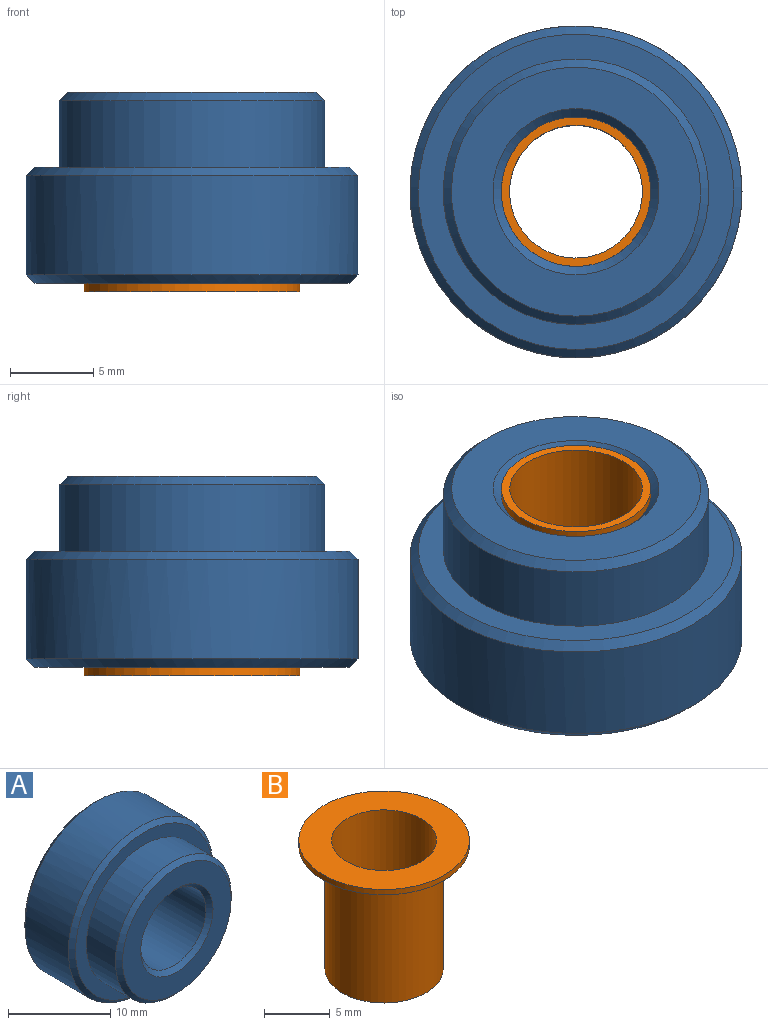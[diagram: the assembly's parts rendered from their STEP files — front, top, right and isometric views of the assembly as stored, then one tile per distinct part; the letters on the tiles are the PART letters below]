
ASSEMBLY  parts=2 mates=1
PART A: 11 faces, bbox 20x11.5x20 mm
  f0: plane 15x15mm, normal (0,-1,0), area 98.2mm2, adj f6,f9
  f1: cylinder r=4.5mm len=10.5mm, axis (0,-1,0), area 296.9mm2, adj f9,f10
  f2: plane 19x19mm, normal (0,1,0), area 205mm2, adj f7,f10
  f3: cylinder r=10mm len=20mm, axis (0,-1,0), area 377mm2, adj f7,f8
  f4: plane 19x19mm, normal (0,-1,0), area 82.5mm2, adj f5,f8
  f5: cylinder r=8mm len=16mm, axis (0,-1,0), area 201.1mm2, adj f4,f6
  f6: cone r=7.5mm half-angle=45deg, axis (0,1,0), area 34.4mm2, adj f0,f5
  f7: cone r=10mm half-angle=45deg, axis (0,-1,0), area 43.3mm2, adj f2,f3
  f8: cone r=9.5mm half-angle=45deg, axis (0,1,0), area 43.3mm2, adj f3,f4
  f9: cone r=4.5mm half-angle=45deg, axis (0,-1,0), area 21.1mm2, adj f0,f1
  f10: cone r=5mm half-angle=45deg, axis (0,1,0), area 21.1mm2, adj f1,f2
PART B: 6 faces, bbox 13x13x12 mm
  f0: cylinder r=4mm len=12mm, axis (0,0,1), area 301.6mm2, adj f1,f5
  f1: plane 9x9mm, normal (0,0,-1), area 13.4mm2, adj f0,f2
  f2: cylinder r=4.5mm len=11.5mm, axis (0,0,1), area 325.2mm2, adj f1,f3
  f3: plane 13x13mm, normal (0,0,-1), area 69.1mm2, adj f2,f4
  f4: cylinder r=6.5mm len=13mm, axis (0,0,1), area 20.4mm2, adj f3,f5
  f5: plane 13x13mm, normal (0,0,1), area 82.5mm2, adj f0,f4
PLACE A rot(axis=(-1,0,0),90deg) t=(-34.24,16.08,178.06)mm
PLACE B rot(axis=(1,0,0),180deg) t=(-34.24,16.08,178.06)mm
MATE fastened B.f0 <-> A.f1  axis (0,0,1) through (-34.24,16.08,166.56)mm
